# Revit family: Lavatories-Commercial_Round_LT502_TOTO
name_source: partatom
category: Plumbing Fixtures
revit_build: Autodesk Revit Architecture 2013 (Build: 20130531_2115(x64)
units: mm (PartAtom-declared; Revit-internal decimal feet)

## types (1)
- LT502
    04 CSI = 22 42 16
    95 CSI = 15410
    ADA Compliant = Yes
    Assembly Code = D2010310
    Basin Depth = 12 1/2"
    Basin Width = 14 7/8"
    CAD Drawing URL = http://assets.totousa.com
    CW Connection = Yes
    CWFU = 0
    Certifications = IAPMO(cUPC), State of Massachusetts , City of Los Angeles, and others
    Code Compliance = UPC, IPC, NSPC, NPC Canada, and others
    Color Availability = #01 Cotton, #03 Bone, #12 Sedona Beige
    Default Elevation = 0"
    Depth = 19"
    Description = Lavatories, Commercial, Round, Self Rimming Lavatory - Single Hole - ADA
    Finish = Vitreous China - TOTO - 01 Cotton
    HW Connection = Yes
    HWFU = 0
    Height = 10 3/8"
    Industry Standards = Meets and exceeds ASME A112.19.2/CSA B45.1
    Manufacturer = TOTO USA, Inc.
    Manufacturer Fax = (770) 282-0002
    Material = Vitreous China
    Model = LT502
    Mounting = Self-Rimming
    Offset From Countertop = 0"
    Sanitary Connetor = Sanitary Connection
    SanoGloss Available = No
    Shipping Weight = 21.00 lb
    Sink Configuration = Single Sink
    Sink Type = Lavatory
    Spec Sheet URL = http://assets.totousa.com
    Style = Commercial
    Subcategory = Lavatories
    Toto BIM Number = BM-00239
    URL = http://www.totousa.com
    Vent Connection = Yes
    WFU = 0
    Warranty = One Year Limited Warranty
    Warranty URL = http://www.totousa.com
    Waste Connection = Yes
    Waste Connection NPT Radius = 5/8"
    Width = 19"
    ecoScorecard Product Page = http://toto.ecoscorecard.com
    ecoScorecard_data = http://toto.ecoscorecard.com

## geometry (parser evidence)
native form markers: Blend x8, Sweep x3
no freeform markers — native parametric forms only
